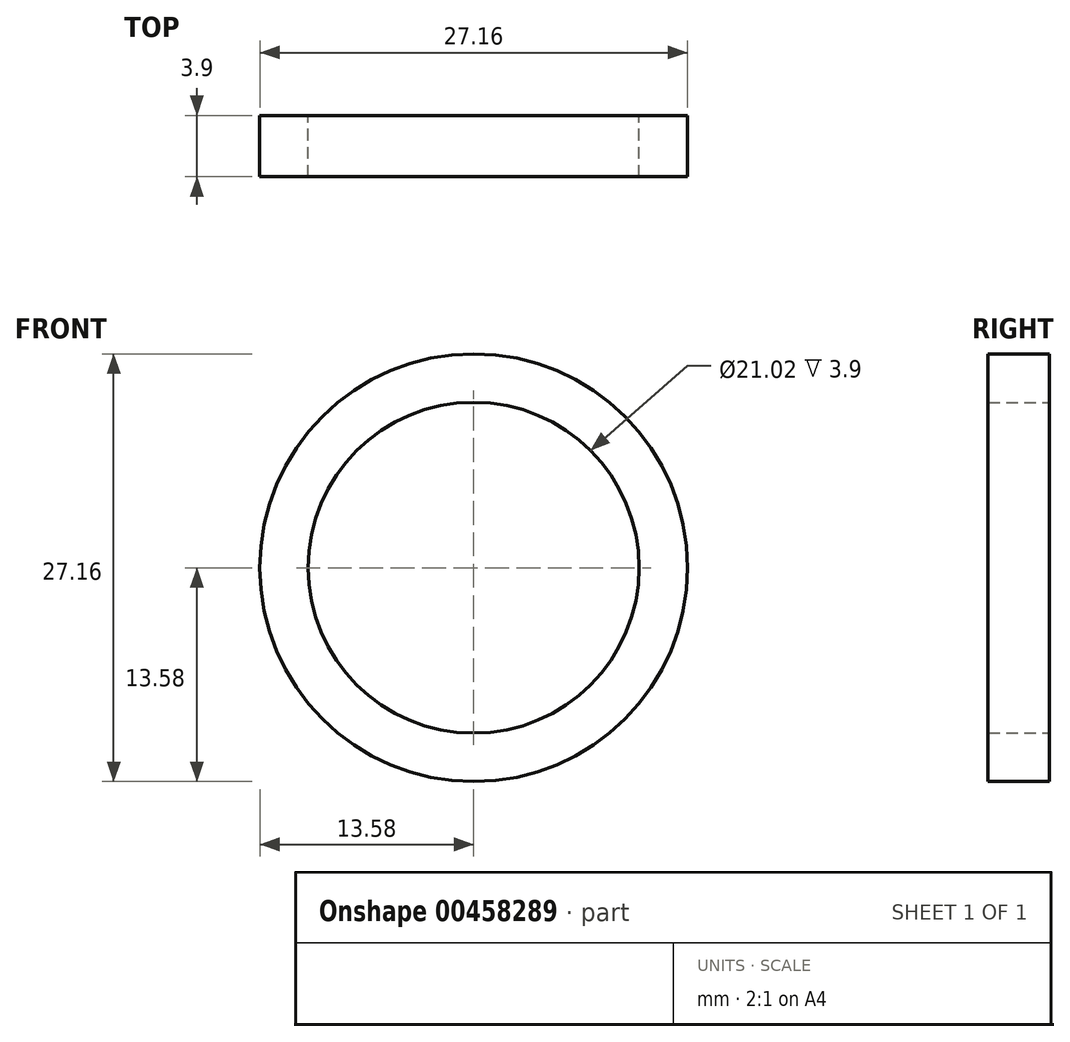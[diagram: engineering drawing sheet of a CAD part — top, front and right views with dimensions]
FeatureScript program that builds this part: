
annotation { "Feature Type Name" : "Feature", "Feature Type Description" : "" }
export const myFeature = defineFeature(function(context is Context, id is Id, definition is map)
    precondition{}
    {
        {
            var Q0;
            Q0=qCreatedBy(makeId("Front.planeOp"),FACE);
            var sketch = newSketch(context, id + "F0", { "sketchPlane" : qUnion([Q0])});
            skCircle(sketch, "E0", {"center": v(0, 0) * mm, "radius": 13.58 * mm});
            skCircle(sketch, "E1", {"center": v(0, 0) * mm, "radius": 10.5 * mm});
            skSolve(sketch);
        }
        {
            var Q0;
            Q0 = qSketchRegion(id + "F0", true);
            extrude(context, id + "F1", {"entities" : qUnion([Q0]), "depth" : 3.9 * mm});
        }
    });
